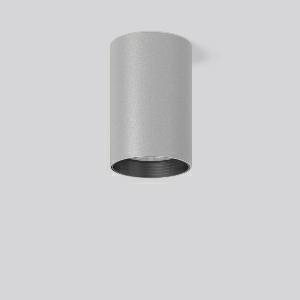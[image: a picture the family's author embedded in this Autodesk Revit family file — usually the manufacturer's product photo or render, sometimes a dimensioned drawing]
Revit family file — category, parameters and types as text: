
# Revit family: heledon_maxi_a_931242_004_e724
name_source: partatom
category: Lighting Fixtures
units: mm (PartAtom-declared; Revit-internal decimal feet)

## family parameters
Cut with Voids When Loaded = No
Host = Face
Light Source = No
Part Type = Normal
Room Calculation Point = No
Round Connector Dimension = Use Diameter
Shared = No

## types (1)
- HELEDON maxi A (1 x LED Modul 920 meat+, 1850 lm, 2000)
    Apparent Load = 33 VA
    Approval mark = CE
    CIE Flux Codes = 96 99 100 100 100
    Color Rendering = 90
    Color Temperature = 2000
    Default Elevation = 1800 mm
    Description = Series: HELEDON maxi
Cylindrical surface-mounted downlight. Housing: die-cast aluminium, powder-coated. Internal ceiling frame polycarbonate with bayonet mounting. Black plastic ring and recessed LED to prevent glare from the side. Optical assembly with lens made of plastic (polycarbonate) for the best homogeneous light distribution - can be changed without tools. Special LED for illumination of meat included. Suitable for Ceiling mounting. Easy installation with a separate ceiling frame with bayonet mounting and plug connection. Driver integrated. Connected via plug-in connector. High quality converter without flickering and stroboscopic effect. The following accessories can be mounted without use of tools: interchangeable lenses, decorative glasses, honeycomb louvre, clear and frosted diffusers, white interchangeable plastic ring. 
Colour: silver
Diameter: 123 mm
Height: 183 mm
Lamp: LED
Socket: without socket
Colour temperature: meat +
System power: 33 W
Rated luminous flux: 1850 lm
Luminous efficiency: 56 lm/W
Control gear: Regulated power supply
Protection class: I
Type of protection: IP 20
    Height = 183 mm
    Lamp = 1 x LED Modul 920 meat+
    Lamp Light Flux = 1850 lm
    Lamp count = 1
    Length = 123 mm
    Lifetime = 50000 h
    Luminous efficacy = 56 lm/W
    Manufacturer = RZB
    ModVariant = No
    Model = 931242.004
    Mounting Place = Ceiling
    Mounting Type = Surface mounted
    Number of Poles = 1
    OnlyDefault = Yes
    Power Factor = 1
    Product Name = HELEDON maxi A
    Product group = Surface mounted downlights
    ProductGroupID = 302
    Protection Class = Protection class I
    Protection Degree = IP 20
    RLX_Detail_Level = 1
    RLX_Emergency_Light_Flux = 0 lm
    RLX_Emergency_Type = 0
    RLX_Emergency_Type_DB = No
    RlxData = <blob elided: 99645 chars, md5=d9b79204>
    Socket = socket
    Standby Power = 0 W
    System Light Flux = 1850 lm
    System Power = 33 W
    Type Comments = Product without accessories
    Type Image = 931193.004.jpg
    URL = http://relux.com
    VarID = ---
    Voltage = 230 V
    Voltage Range = 220-240 V
    Weight = 0.00 kg
    Width = 0 mm  [stored 0 ft]

note: [stored X ft] marks values corroborated as IEEE doubles in the binary element streams (Revit-internal decimal feet)

## geometry (parser evidence)
native form markers: Blend x4, Sweep x10
no freeform markers — native parametric forms only
